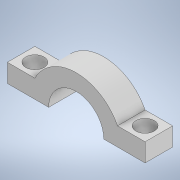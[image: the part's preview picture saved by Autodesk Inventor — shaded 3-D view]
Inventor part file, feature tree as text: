
AUTODESK INVENTOR PART (.ipt)
format: ipt  version: 2020 (Build 240168000, 168)  size: 124,928 bytes
history: native  units: in
note: dims shown in document units (in); Inventor stores cm internally (conversion verified against a paired STEP export)
features: extrude x3, sketch x3
ambient origin geometry x8: Origin, YZ Plane, XZ Plane, XY Plane, X Axis, Y Axis, Z Axis, Center Point
bodies: Solid1 (feature_tree)
feature tree (6):
  extrude  "Extrusion1"  Depth=0.3937in TaperAngle=0.0deg
  extrude  "Extrusion2"  Depth=0.2362in
  extrude  "Extrusion3"  Depth=0.2362in
  sketch  "Sketch1"  dims[d0=1.1811in d1=0.3937in d2=0.0in]
  sketch  "Sketch2"  dims[d3=0.4724in d4=0.2362in]
  sketch  "Sketch3"  dims[d5=0.2362in d6=0.2362in d7=0.3937in d8=0.0in d9=0.1575in d10=0.1575in d11=0.3937in d12=0.0in]
